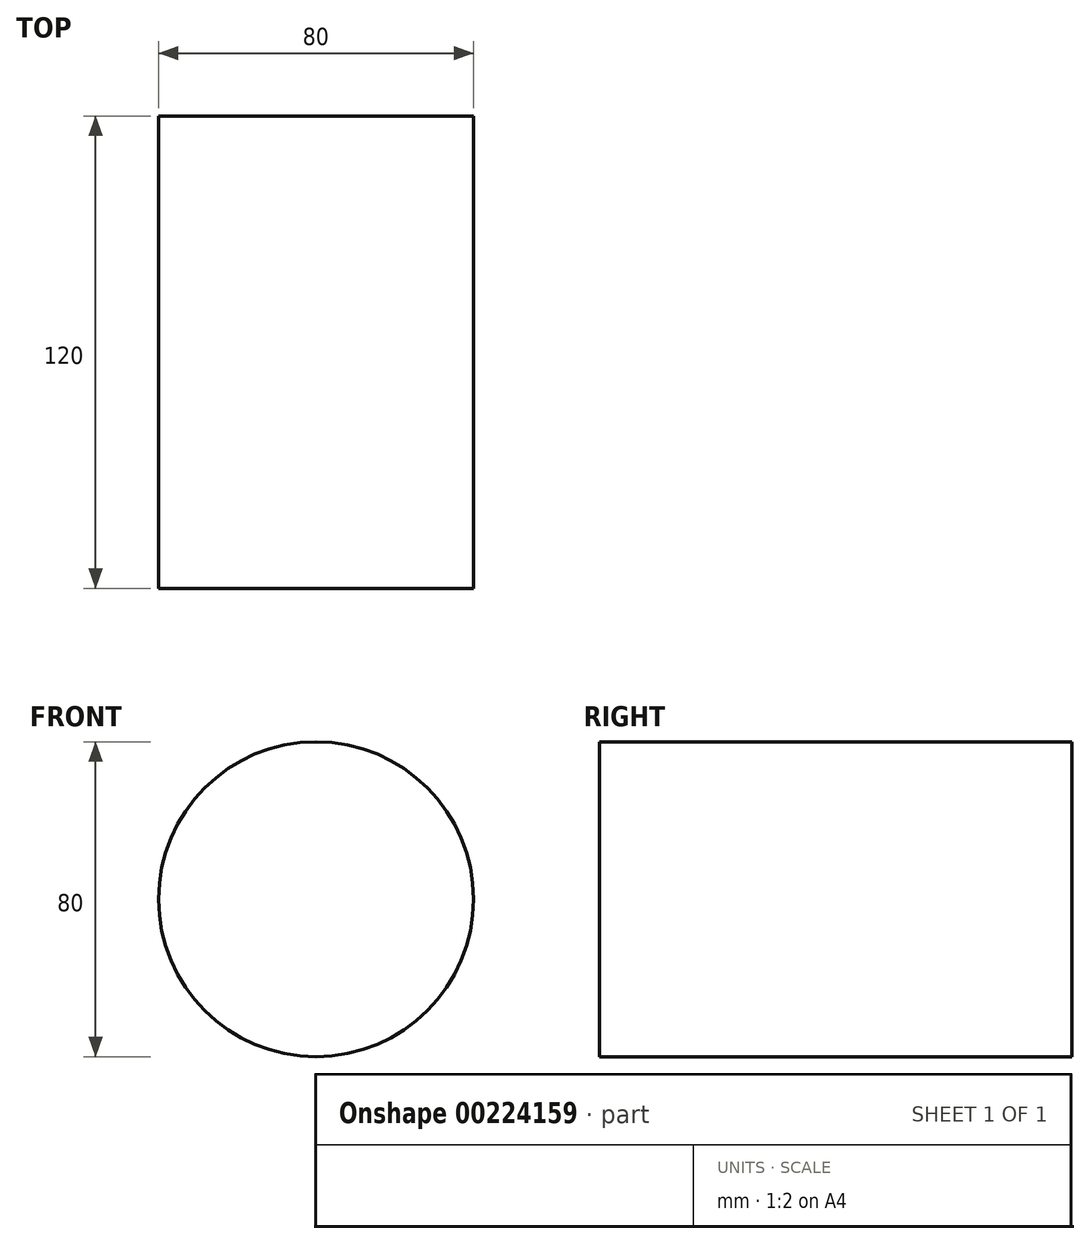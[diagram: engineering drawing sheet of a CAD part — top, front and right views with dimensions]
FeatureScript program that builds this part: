
annotation { "Feature Type Name" : "Feature", "Feature Type Description" : "" }
export const myFeature = defineFeature(function(context is Context, id is Id, definition is map)
    precondition{}
    {
        {
            var Q0;
            Q0=qCreatedBy(makeId("Front.planeOp"),FACE);
            var sketch = newSketch(context, id + "F0", { "sketchPlane" : qUnion([Q0])});
            skCircle(sketch, "E0", {"center": v(0, 0) * mm, "radius": 40 * mm});
            skSolve(sketch);
        }
        {
            var Q0;
            Q0=makeQuery(id+"F0.imprint","IMPRINT",FACE,{"disambiguationData":[TD([[makeQuery(id+"F0.imprint","IMPRINT",EDGE,{"derivedFrom":sQuery(id+"F0.wireOp",EDGE,"E0")}),1.0]])]});
            extrude(context, id + "F1", {"entities" : qUnion([Q0]), "depth" : 120 * mm});
        }
    });
